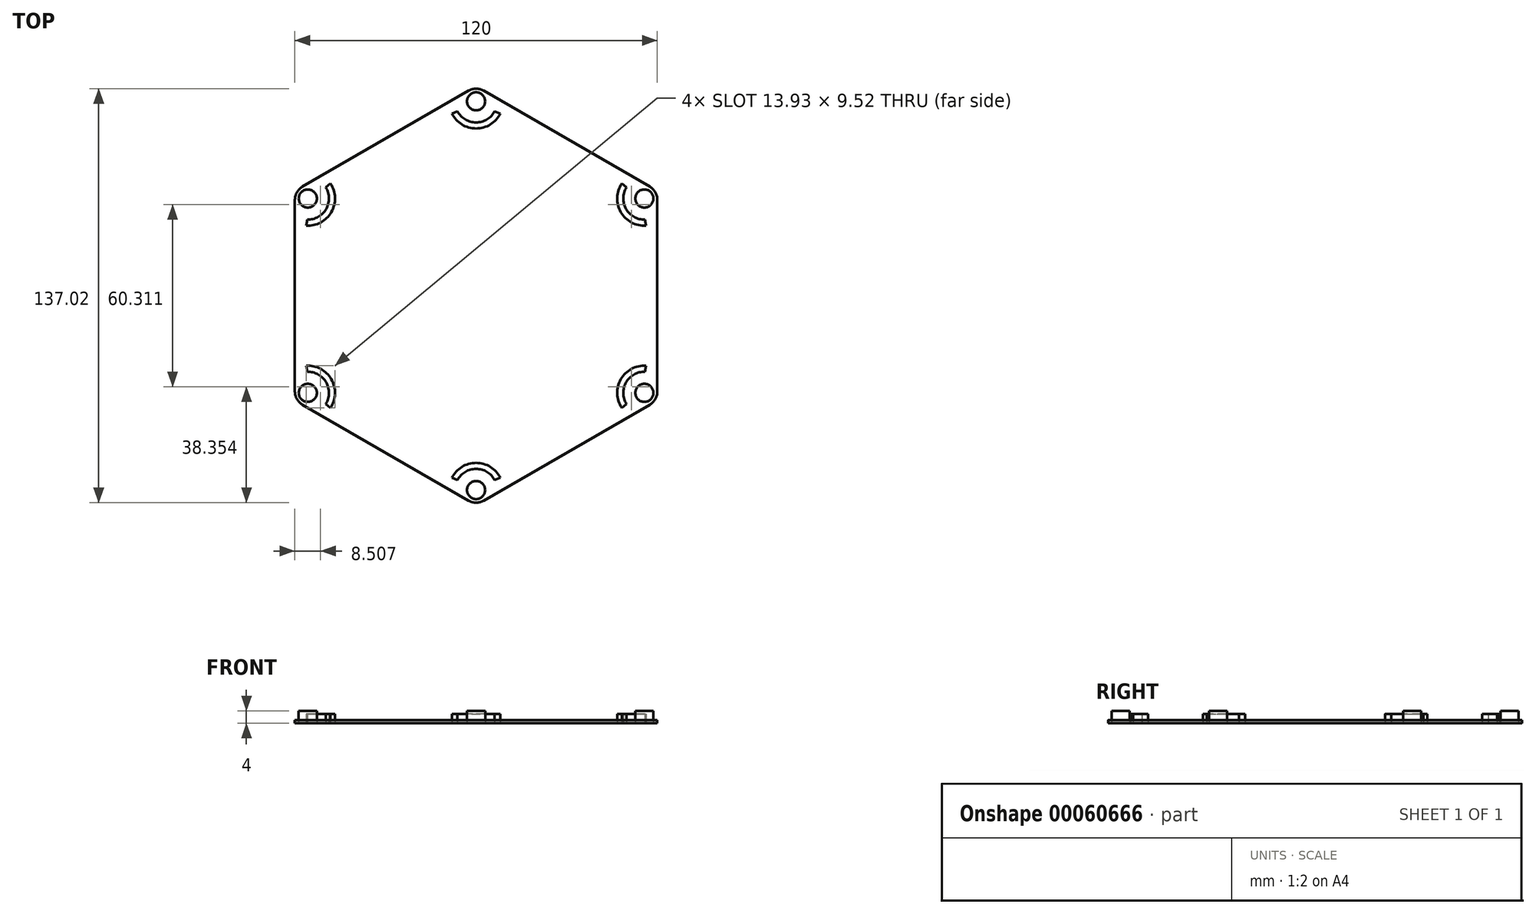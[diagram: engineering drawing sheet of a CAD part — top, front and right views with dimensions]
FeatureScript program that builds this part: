
annotation { "Feature Type Name" : "Feature", "Feature Type Description" : "" }
export const myFeature = defineFeature(function(context is Context, id is Id, definition is map)
    precondition{}
    {
        {
            var Q0;
            Q0=qCreatedBy(makeId("Top.planeOp"),FACE);
            var sketch = newSketch(context, id + "F0", { "sketchPlane" : qUnion([Q0])});
            skCircle(sketch, "E0.cCircle", {"center": v(0, 0) * mm, "radius": 60 * mm, "construction": true});
            skLineSegment(sketch, "E0.0", {"start": v(60, 31.75) * mm, "end": v(60, -31.75) * mm});
            skLineSegment(sketch, "E0.1", {"start": v(57.5, -36.08) * mm, "end": v(2.5, -67.84) * mm});
            skLineSegment(sketch, "E0.2", {"start": v(-2.5, -67.84) * mm, "end": v(-57.5, -36.08) * mm});
            skLineSegment(sketch, "E0.3", {"start": v(-60, -31.75) * mm, "end": v(-60, 31.75) * mm});
            skLineSegment(sketch, "E0.4", {"start": v(-57.5, 36.08) * mm, "end": v(-2.5, 67.84) * mm});
            skLineSegment(sketch, "E0.5", {"start": v(2.5, 67.84) * mm, "end": v(57.5, 36.08) * mm});
            skPoint(sketch, "E0.0.midPoint", {"position": v(60, 0) * mm});
            skCircle(sketch, "E1", {"center": v(0, -64.35) * mm, "radius": 3 * mm});
            skPoint(sketch, "E2.visualSharp", {"position": v(0, -69.28) * mm});
            skArc(sketch, "E2.filletArc", {"start": v(-2.5, -67.84) * mm, "mid": v(0, -68.5) * mm, "end": v(2.5, -67.84) * mm});
            skPoint(sketch, "E3.visualSharp", {"position": v(60, -34.64) * mm});
            skArc(sketch, "E3.filletArc", {"start": v(57.5, -36.08) * mm, "mid": v(59.33, -34.25) * mm, "end": v(60, -31.75) * mm});
            skPoint(sketch, "E4.visualSharp", {"position": v(-60, -34.64) * mm});
            skArc(sketch, "E4.filletArc", {"start": v(-60, -31.75) * mm, "mid": v(-59.33, -34.25) * mm, "end": v(-57.5, -36.08) * mm});
            skPoint(sketch, "E5.visualSharp", {"position": v(60, 34.64) * mm});
            skArc(sketch, "E5.filletArc", {"start": v(60, 31.75) * mm, "mid": v(59.33, 34.25) * mm, "end": v(57.5, 36.08) * mm});
            skPoint(sketch, "E6.visualSharp", {"position": v(-60, 34.64) * mm});
            skArc(sketch, "E6.filletArc", {"start": v(-57.5, 36.08) * mm, "mid": v(-59.33, 34.25) * mm, "end": v(-60, 31.75) * mm});
            skPoint(sketch, "E7.visualSharp", {"position": v(0, 69.28) * mm});
            skArc(sketch, "E7.filletArc", {"start": v(2.5, 67.84) * mm, "mid": v(0, 68.5) * mm, "end": v(-2.5, 67.84) * mm});
            skArc(sketch, "E8.0", {"start": v(6.15, -61.01) * mm, "mid": v(0, -57.35) * mm, "end": v(-6.15, -61.01) * mm});
            skArc(sketch, "E9.0", {"start": v(8.04, -60.31) * mm, "mid": v(0, -55.35) * mm, "end": v(-8.04, -60.31) * mm});
            skLineSegment(sketch, "E10.0", {"start": v(6.15, -61.01) * mm, "end": v(8.04, -60.31) * mm});
            skLineSegment(sketch, "E11.MirrorCS", {"start": v(-6.15, -61.01) * mm, "end": v(-8.04, -60.31) * mm});
            skCircle(sketch, "E12.1.0", {"center": v(-55.73, -32.18) * mm, "radius": 3 * mm});
            skArc(sketch, "E12.1.1", {"start": v(-49.76, -35.83) * mm, "mid": v(-49.67, -28.68) * mm, "end": v(-55.91, -25.18) * mm});
            skArc(sketch, "E12.1.2", {"start": v(-48.2, -37.12) * mm, "mid": v(-47.94, -27.68) * mm, "end": v(-56.25, -23.2) * mm});
            skLineSegment(sketch, "E12.1.3", {"start": v(-49.76, -35.83) * mm, "end": v(-48.2, -37.12) * mm});
            skLineSegment(sketch, "E12.1.4", {"start": v(-55.91, -25.18) * mm, "end": v(-56.25, -23.2) * mm});
            skCircle(sketch, "E12.2.0", {"center": v(-55.73, 32.18) * mm, "radius": 3 * mm});
            skArc(sketch, "E12.2.1", {"start": v(-55.91, 25.18) * mm, "mid": v(-49.67, 28.68) * mm, "end": v(-49.76, 35.83) * mm});
            skArc(sketch, "E12.2.2", {"start": v(-56.25, 23.2) * mm, "mid": v(-47.94, 27.68) * mm, "end": v(-48.2, 37.12) * mm});
            skLineSegment(sketch, "E12.2.3", {"start": v(-55.91, 25.18) * mm, "end": v(-56.25, 23.2) * mm});
            skLineSegment(sketch, "E12.2.4", {"start": v(-49.76, 35.83) * mm, "end": v(-48.2, 37.12) * mm});
            skCircle(sketch, "E12.3.0", {"center": v(0, 64.35) * mm, "radius": 3 * mm});
            skArc(sketch, "E12.3.1", {"start": v(-6.15, 61.01) * mm, "mid": v(0, 57.35) * mm, "end": v(6.15, 61.01) * mm});
            skArc(sketch, "E12.3.2", {"start": v(-8.04, 60.31) * mm, "mid": v(0, 55.35) * mm, "end": v(8.04, 60.31) * mm});
            skLineSegment(sketch, "E12.3.3", {"start": v(-6.15, 61.01) * mm, "end": v(-8.04, 60.31) * mm});
            skLineSegment(sketch, "E12.3.4", {"start": v(6.15, 61.01) * mm, "end": v(8.04, 60.31) * mm});
            skCircle(sketch, "E12.4.0", {"center": v(55.73, 32.18) * mm, "radius": 3 * mm});
            skArc(sketch, "E12.4.1", {"start": v(49.76, 35.83) * mm, "mid": v(49.67, 28.68) * mm, "end": v(55.91, 25.18) * mm});
            skArc(sketch, "E12.4.2", {"start": v(48.2, 37.12) * mm, "mid": v(47.94, 27.68) * mm, "end": v(56.25, 23.2) * mm});
            skLineSegment(sketch, "E12.4.3", {"start": v(49.76, 35.83) * mm, "end": v(48.2, 37.12) * mm});
            skLineSegment(sketch, "E12.4.4", {"start": v(55.91, 25.18) * mm, "end": v(56.25, 23.2) * mm});
            skCircle(sketch, "E12.5.0", {"center": v(55.73, -32.18) * mm, "radius": 3 * mm});
            skArc(sketch, "E12.5.1", {"start": v(55.91, -25.18) * mm, "mid": v(49.67, -28.68) * mm, "end": v(49.76, -35.83) * mm});
            skArc(sketch, "E12.5.2", {"start": v(56.25, -23.2) * mm, "mid": v(47.94, -27.68) * mm, "end": v(48.2, -37.12) * mm});
            skLineSegment(sketch, "E12.5.3", {"start": v(55.91, -25.18) * mm, "end": v(56.25, -23.2) * mm});
            skLineSegment(sketch, "E12.5.4", {"start": v(49.76, -35.83) * mm, "end": v(48.2, -37.12) * mm});
            skLineSegment(sketch, "E12.anchor1", {"start": v(0, 0) * mm, "end": v(0, -64.35) * mm, "construction": true});
            skLineSegment(sketch, "E12.anchor2", {"start": v(0, 0) * mm, "end": v(55.73, -32.18) * mm, "construction": true});
            skSolve(sketch);
        }
        {
            var Q0;
            Q0=qSketchRegion(id+"F0",true);
            extrude(context, id + "F1", {"entities" : qUnion([Q0]), "depth" : 1 * mm});
        }
        {
            var Q0;
            Q0=makeQuery(id+"F0.imprint","IMPRINT",FACE,{"disambiguationData":[TD([[makeQuery(id+"F0.imprint","IMPRINT",EDGE,{"derivedFrom":sQuery(id+"F0.wireOp",EDGE,"E8.0")}),-1.0]])]});
            var Q1;
            Q1=makeQuery(id+"F0.imprint","IMPRINT",FACE,{"disambiguationData":[TD([[makeQuery(id+"F0.imprint","IMPRINT",EDGE,{"derivedFrom":sQuery(id+"F0.wireOp",EDGE,"E12.1.1")}),-1.0]])]});
            var Q2;
            Q2=makeQuery(id+"F0.imprint","IMPRINT",FACE,{"disambiguationData":[TD([[makeQuery(id+"F0.imprint","IMPRINT",EDGE,{"derivedFrom":sQuery(id+"F0.wireOp",EDGE,"E12.5.1")}),-1.0]])]});
            var Q3;
            Q3=makeQuery(id+"F0.imprint","IMPRINT",FACE,{"disambiguationData":[TD([[makeQuery(id+"F0.imprint","IMPRINT",EDGE,{"derivedFrom":sQuery(id+"F0.wireOp",EDGE,"E12.2.1")}),-1.0]])]});
            var Q4;
            Q4=makeQuery(id+"F0.imprint","IMPRINT",FACE,{"disambiguationData":[TD([[makeQuery(id+"F0.imprint","IMPRINT",EDGE,{"derivedFrom":sQuery(id+"F0.wireOp",EDGE,"E12.3.1")}),-1.0]])]});
            var Q5;
            Q5=makeQuery(id+"F0.imprint","IMPRINT",FACE,{"disambiguationData":[TD([[makeQuery(id+"F0.imprint","IMPRINT",EDGE,{"derivedFrom":sQuery(id+"F0.wireOp",EDGE,"E12.4.1")}),-1.0]])]});
            extrude(context, id + "F2", {"entities" : qUnion([Q0, Q1, Q2, Q3, Q4, Q5]), "depth" : 3 * mm});
        }
        {
            var Q0;
            Q0=makeQuery(id+"F0.imprint","IMPRINT",FACE,{"disambiguationData":[TD([[makeQuery(id+"F0.imprint","IMPRINT",EDGE,{"derivedFrom":sQuery(id+"F0.wireOp",EDGE,"E12.1.0")}),1.0]])]});
            var Q1;
            Q1=makeQuery(id+"F0.imprint","IMPRINT",FACE,{"disambiguationData":[TD([[makeQuery(id+"F0.imprint","IMPRINT",EDGE,{"derivedFrom":sQuery(id+"F0.wireOp",EDGE,"E1")}),1.0]])]});
            var Q2;
            Q2=makeQuery(id+"F0.imprint","IMPRINT",FACE,{"disambiguationData":[TD([[makeQuery(id+"F0.imprint","IMPRINT",EDGE,{"derivedFrom":sQuery(id+"F0.wireOp",EDGE,"E12.5.0")}),1.0]])]});
            var Q3;
            Q3=makeQuery(id+"F0.imprint","IMPRINT",FACE,{"disambiguationData":[TD([[makeQuery(id+"F0.imprint","IMPRINT",EDGE,{"derivedFrom":sQuery(id+"F0.wireOp",EDGE,"E12.4.0")}),1.0]])]});
            var Q4;
            Q4=makeQuery(id+"F0.imprint","IMPRINT",FACE,{"disambiguationData":[TD([[makeQuery(id+"F0.imprint","IMPRINT",EDGE,{"derivedFrom":sQuery(id+"F0.wireOp",EDGE,"E12.3.0")}),1.0]])]});
            var Q5;
            Q5=makeQuery(id+"F0.imprint","IMPRINT",FACE,{"disambiguationData":[TD([[makeQuery(id+"F0.imprint","IMPRINT",EDGE,{"derivedFrom":sQuery(id+"F0.wireOp",EDGE,"E12.2.0")}),1.0]])]});
            extrude(context, id + "F3", {"entities" : qUnion([Q0, Q1, Q2, Q3, Q4, Q5]), "depth" : 4 * mm});
        }
    });
